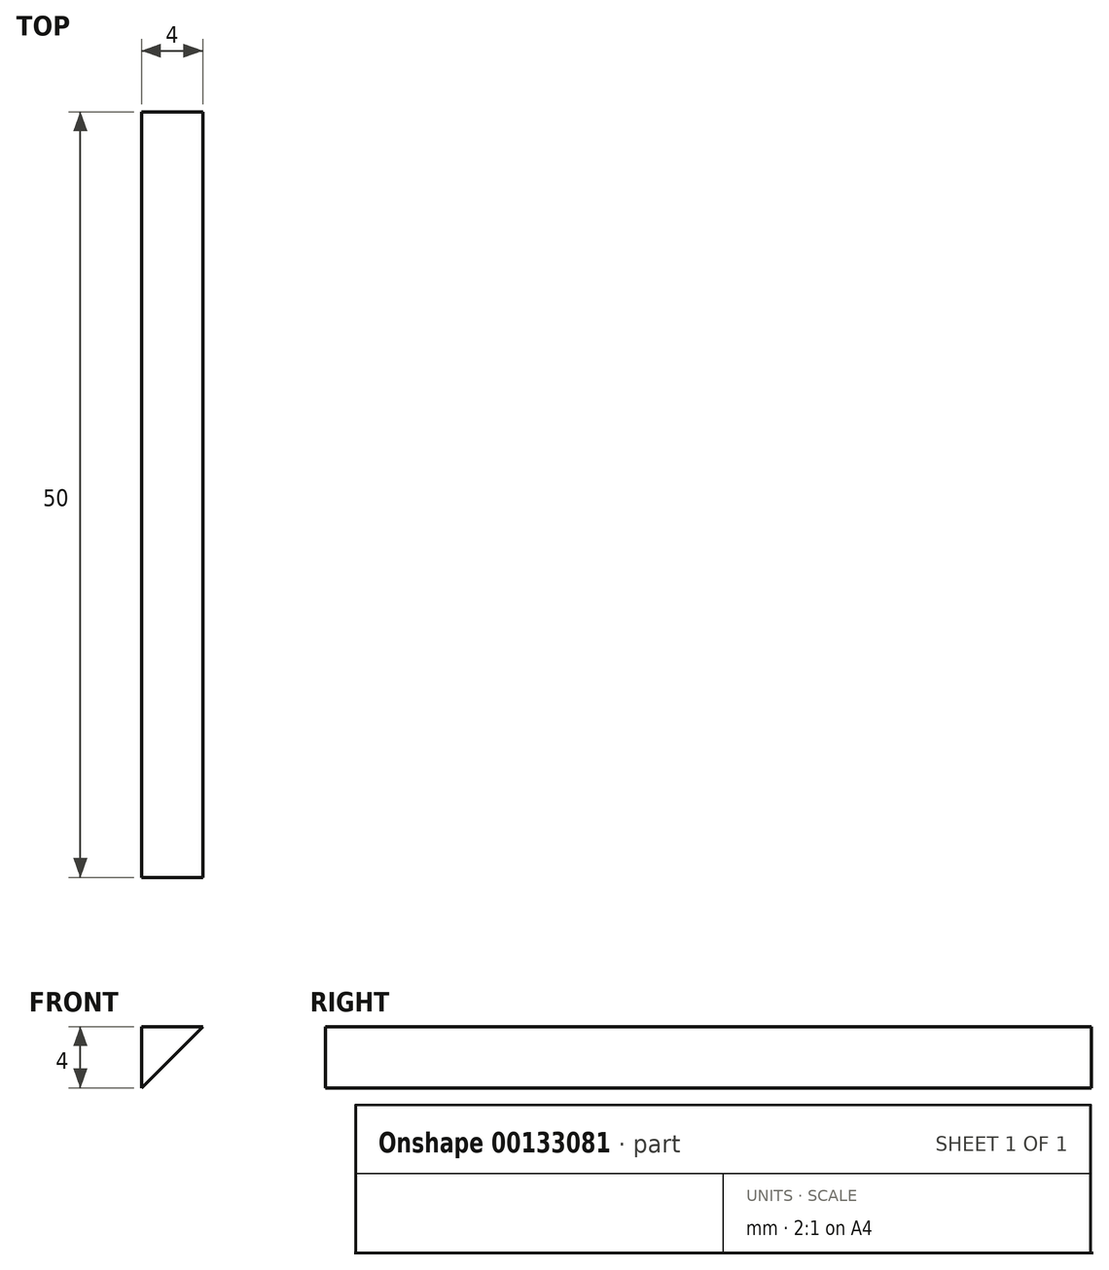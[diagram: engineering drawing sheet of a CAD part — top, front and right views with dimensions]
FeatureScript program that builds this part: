
annotation { "Feature Type Name" : "Feature", "Feature Type Description" : "" }
export const myFeature = defineFeature(function(context is Context, id is Id, definition is map)
    precondition{}
    {
        {
            var Q0;
            Q0=qCreatedBy(makeId("Front.planeOp"),FACE);
            var sketch = newSketch(context, id + "F0", { "sketchPlane" : qUnion([Q0])});
            skLineSegment(sketch, "E0", {"start": v(-37.07, 22.52) * mm, "end": v(-37.07, 18.52) * mm});
            skLineSegment(sketch, "E1", {"start": v(-37.07, 18.52) * mm, "end": v(-33.07, 22.52) * mm});
            skLineSegment(sketch, "E2", {"start": v(-33.07, 22.52) * mm, "end": v(-37.07, 22.52) * mm});
            skSolve(sketch);
        }
        {
            var Q0;
            Q0 = qSketchRegion(id + "F0", true);
            extrude(context, id + "F1", {"entities" : qUnion([Q0]), "depth" : 50 * mm});
        }
    });
